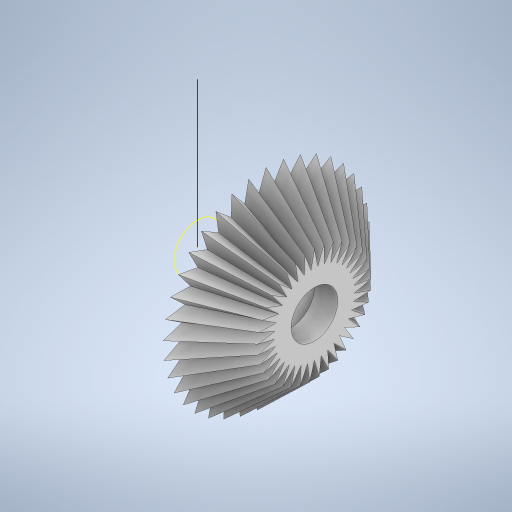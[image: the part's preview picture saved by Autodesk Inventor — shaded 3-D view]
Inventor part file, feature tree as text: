
AUTODESK INVENTOR PART (.ipt)
format: ipt  version: 2023 (Build 270158030, 158C)  size: 585,216 bytes
history: native  units: in
note: dims shown in document units (in); Inventor stores cm internally (conversion verified against a paired STEP export)
features: sketch x7, extrude x4, other x2, pattern_circular x2, loft x1
ambient origin geometry x8: Origin, YZ Plane, XZ Plane, XY Plane, X Axis, Y Axis, Z Axis, Center Point
bodies: Solid1 (feature_tree)
feature tree (16):
  other  "Main Body"
  extrude  "Teeth"  TaperAngle=45.0deg  [1 undecoded]
  pattern_circular  "Circular Pattern1"  Count=5  [1 undecoded]
  loft  "Angle Teeth"
  pattern_circular  "Circular Pattern2"  Count=2  [1 undecoded]
  extrude  "Extrusion4"  TaperAngle=0.0deg  [1 undecoded]
  sketch  "Sketch13"  dims[d22=14.5669in d23=360.0deg d25=0.0in d26=90.0deg]
  extrude  "Extrusion5"  Depth=14.5669in TaperAngle=360.0deg
  extrude  "Extrusion6"  TaperAngle=0.0deg  [1 undecoded]
  sketch  "Sketch1"  dims[d0=0.7874in d1=45.0deg]
  sketch  "Sketch6"  dims[d2=0.5906in d3=1.9685in]
  sketch  "Sketch11"  dims[d4=90.0deg d18=45.0deg]
  other  "Edges2"
  sketch  "Sketch12"  dims[d19=0.3937in d20=0.7874in d21=0.0in]
  sketch  "Sketch14"  dims[d27=0.0in d28=90.0deg d29=14.5669in d30=360.0deg]
  sketch  "Sketch15"  dims[d32=0.5906in d33=0.0in d34=0.0in d35=0.8661in d36=0.0in d37=1.0236in d38=0.315in d39=0.0in]
note: 5 required parameter values undecoded (feature->parameter linkage not recoverable at this tier; creation-order binding heuristic only, values carry confidence <= 0.55)
